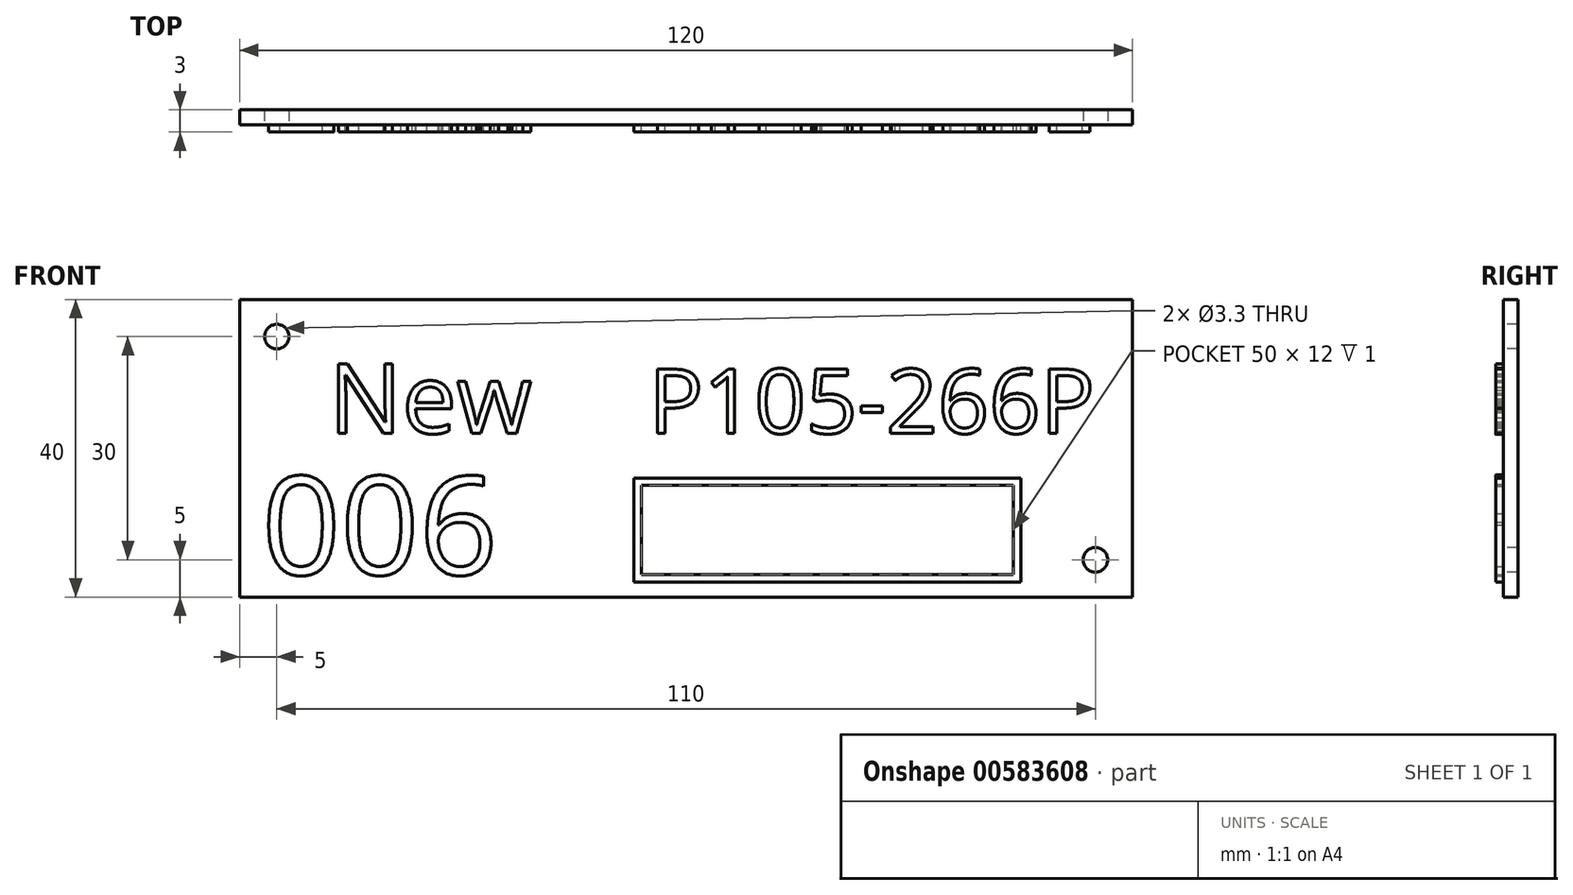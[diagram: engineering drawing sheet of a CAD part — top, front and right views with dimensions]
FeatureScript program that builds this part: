
annotation { "Feature Type Name" : "Feature", "Feature Type Description" : "" }
export const myFeature = defineFeature(function(context is Context, id is Id, definition is map)
    precondition{}
    {
        {
            var Q0;
            Q0=qCreatedBy(makeId("Front.planeOp"),FACE);
            var sketch = newSketch(context, id + "F0", { "sketchPlane" : qUnion([Q0])});
            skLineSegment(sketch, "E0.bottom", {"start": v(60, -20) * mm, "end": v(-60, -20) * mm});
            skLineSegment(sketch, "E0.top", {"start": v(60, 20) * mm, "end": v(-60, 20) * mm});
            skLineSegment(sketch, "E0.left", {"start": v(60, -20) * mm, "end": v(60, 20) * mm});
            skLineSegment(sketch, "E0.right", {"start": v(-60, -20) * mm, "end": v(-60, 20) * mm});
            skPoint(sketch, "E0.middle", {"position": v(0, 0) * mm});
            skSolve(sketch);
        }
        {
            var Q0;
            Q0=makeQuery(id+"F0.imprint","IMPRINT",FACE,{"disambiguationData":[TD([[makeQuery(id+"F0.imprint","IMPRINT",EDGE,{"derivedFrom":sQuery(id+"F0.wireOp",EDGE,"E0.bottom")}),-1.0]])]});
            extrude(context, id + "F1", {"entities" : qUnion([Q0]), "depth" : 2 * mm});
        }
        {
            var Q0;
            Q0=makeQuery(id+"F1.opExtrude","CAP_FACE",FACE,{"disambiguationData":[OSD([sQuery(id+"F0.wireOp",EDGE,"E0.bottom"),sQuery(id+"F0.wireOp",EDGE,"E0.top"),sQuery(id+"F0.wireOp",EDGE,"E0.left"),sQuery(id+"F0.wireOp",EDGE,"E0.right")])],"isStart":false});
            var sketch = newSketch(context, id + "F2", { "sketchPlane" : qUnion([Q0])});
            skPoint(sketch, "E1", {"position": v(-55, 15) * mm});
            skPoint(sketch, "E2", {"position": v(55, -15) * mm});
            skSolve(sketch);
        }
        {
            var Q0;
            Q0=sQuery(id+"F2.wireOp",VERTEX,"E1");
            var Q1;
            Q1=sQuery(id+"F2.wireOp",VERTEX,"E2");
            var Q2;
            Q2=makeQuery(id+"F1.opExtrude","SWEPT_BODY",BODY,{"disambiguationData":[OSD([sQuery(id+"F0.wireOp",EDGE,"E0.bottom"),sQuery(id+"F0.wireOp",EDGE,"E0.top"),sQuery(id+"F0.wireOp",EDGE,"E0.left"),sQuery(id+"F0.wireOp",EDGE,"E0.right")])]});
            hole(context, id + "F3", {"style" : HoleStyle.SIMPLE, "endStyle" : HoleEndStyle.THROUGH, "holeDiameter" : 3.3 * mm, "locations" : qUnion([Q0, Q1]), "scope" : qUnion([Q2]), "isTappedThrough" : true});
        }
        {
            var Q0;
            Q0=makeQuery(id+"F1.opExtrude","CAP_FACE",FACE,{"disambiguationData":[OSD([sQuery(id+"F0.wireOp",EDGE,"E0.bottom"),sQuery(id+"F0.wireOp",EDGE,"E0.top"),sQuery(id+"F0.wireOp",EDGE,"E0.left"),sQuery(id+"F0.wireOp",EDGE,"E0.right")])],"isStart":false});
            var sketch = newSketch(context, id + "F4", { "sketchPlane" : qUnion([Q0])});
            skText(sketch, "E3", { "text": "P105-266P", "fontName": "OpenSans-Regular.ttf"});
            const initialGuessF4  = {"E3": [-0.005, 0.002, 1, 0, 0.0087]};
            skSetInitialGuess(sketch, initialGuessF4);
            skSolve(sketch);
        }
        {
            var Q0;
            Q0=qSketchRegion(id+"F4",true);
            extrude(context, id + "F5", {"entities" : qUnion([Q0]), "operationType" : NewBodyOperationType.ADD, "depth" : 1 * mm, "offsetDistance" : 25 * mm});
        }
        {
            var Q0;
            {var subQ0=sQuery(id+"F0.wireOp",EDGE,"E0.top");var subQ1=sQuery(id+"F0.wireOp",EDGE,"E0.left");var subQ2=sQuery(id+"F0.wireOp",EDGE,"E0.right");var subQ3=sQuery(id+"F0.wireOp",EDGE,"E0.bottom");Q0=makeQuery(id+"F5.boolean.opBoolean","SPLIT",FACE,{"disambiguationData":[TD([makeQuery(id+"F1.opExtrude","SWEPT_FACE",FACE,{"disambiguationData":[OSD([subQ3])]})])],"derivedFrom":makeQuery(id+"F1.opExtrude","CAP_FACE",FACE,{"disambiguationData":[OSD([subQ3,subQ0,subQ1,subQ2])],"isStart":false})});}
            var sketch = newSketch(context, id + "F6", { "sketchPlane" : qUnion([Q0])});
            skText(sketch, "E4", { "text": "006", "fontName": "OpenSans-Regular.ttf"});
            const initialGuessF6  = {"E4": [-0.057, -0.017, 1, 0, 0.0133]};
            skSetInitialGuess(sketch, initialGuessF6);
            skSolve(sketch);
        }
        {
            var Q0;
            Q0=qSketchRegion(id+"F6",true);
            extrude(context, id + "F7", {"entities" : qUnion([Q0]), "operationType" : NewBodyOperationType.ADD, "depth" : 1 * mm});
        }
        {
            var Q0;
            {var subQ46=sQuery(id+"F0.wireOp",EDGE,"E0.top");var subQ48=sQuery(id+"F0.wireOp",EDGE,"E0.left");var subQ66=sQuery(id+"F0.wireOp",EDGE,"E0.right");var subQ76=sQuery(id+"F0.wireOp",EDGE,"E0.bottom");var subQ77=makeQuery(id+"F1.opExtrude","SWEPT_FACE",FACE,{"disambiguationData":[OSD([subQ76])]});Q0=makeQuery(id+"F7.boolean.opBoolean","SPLIT",FACE,{"disambiguationData":[TD([subQ77])],"derivedFrom":makeQuery(id+"F5.boolean.opBoolean","SPLIT",FACE,{"disambiguationData":[TD([subQ77])],"derivedFrom":makeQuery(id+"F1.opExtrude","CAP_FACE",FACE,{"disambiguationData":[OSD([subQ76,subQ46,subQ48,subQ66])],"isStart":false})})});}
            var sketch = newSketch(context, id + "F8", { "sketchPlane" : qUnion([Q0])});
            skLineSegment(sketch, "E5.bottom", {"start": v(45, -18) * mm, "end": v(-7, -18) * mm});
            skLineSegment(sketch, "E5.top", {"start": v(45, -4) * mm, "end": v(-7, -4) * mm});
            skLineSegment(sketch, "E5.left", {"start": v(45, -18) * mm, "end": v(45, -4) * mm});
            skLineSegment(sketch, "E5.right", {"start": v(-7, -18) * mm, "end": v(-7, -4) * mm});
            skPoint(sketch, "E5.middle", {"position": v(19, -11) * mm});
            skLineSegment(sketch, "E6.0", {"start": v(44, -5) * mm, "end": v(-6, -5) * mm});
            skLineSegment(sketch, "E6.1", {"start": v(44, -17) * mm, "end": v(44, -5) * mm});
            skLineSegment(sketch, "E6.2", {"start": v(44, -17) * mm, "end": v(-6, -17) * mm});
            skLineSegment(sketch, "E6.3", {"start": v(-6, -17) * mm, "end": v(-6, -5) * mm});
            skSolve(sketch);
        }
        {
            var Q0;
            Q0=makeQuery(id+"F8.imprint","IMPRINT",FACE,{"disambiguationData":[TD([[makeQuery(id+"F8.imprint","IMPRINT",EDGE,{"derivedFrom":sQuery(id+"F8.wireOp",EDGE,"E5.bottom")}),-1.0]])]});
            extrude(context, id + "F9", {"entities" : qUnion([Q0]), "operationType" : NewBodyOperationType.ADD, "depth" : 1 * mm});
        }
        {
            var Q0;
            {var subQ53=sQuery(id+"F0.wireOp",EDGE,"E0.top");var subQ58=sQuery(id+"F0.wireOp",EDGE,"E0.bottom");var subQ59=makeQuery(id+"F1.opExtrude","SWEPT_FACE",FACE,{"disambiguationData":[OSD([subQ58])]});var subQ75=sQuery(id+"F0.wireOp",EDGE,"E0.left");var subQ83=sQuery(id+"F0.wireOp",EDGE,"E0.right");Q0=makeQuery(id+"F9.boolean.opBoolean","SPLIT",FACE,{"disambiguationData":[TD([subQ59])],"derivedFrom":makeQuery(id+"F7.boolean.opBoolean","SPLIT",FACE,{"disambiguationData":[TD([subQ59])],"derivedFrom":makeQuery(id+"F5.boolean.opBoolean","SPLIT",FACE,{"disambiguationData":[TD([subQ59])],"derivedFrom":makeQuery(id+"F1.opExtrude","CAP_FACE",FACE,{"disambiguationData":[OSD([subQ58,subQ53,subQ75,subQ83])],"isStart":false})})})});}
            var sketch = newSketch(context, id + "F10", { "sketchPlane" : qUnion([Q0])});
            skText(sketch, "E7", { "text": "New", "fontName": "OpenSans-Regular.ttf"});
            const initialGuessF10  = {"E7": [-0.048, 0.002, 1, 0, 0.00939]};
            skSetInitialGuess(sketch, initialGuessF10);
            skSolve(sketch);
        }
        {
            var Q0;
            Q0=qSketchRegion(id+"F10",true);
            extrude(context, id + "F11", {"entities" : qUnion([Q0]), "operationType" : NewBodyOperationType.ADD, "depth" : 1 * mm, "offsetDistance" : 25 * mm});
        }
    });
